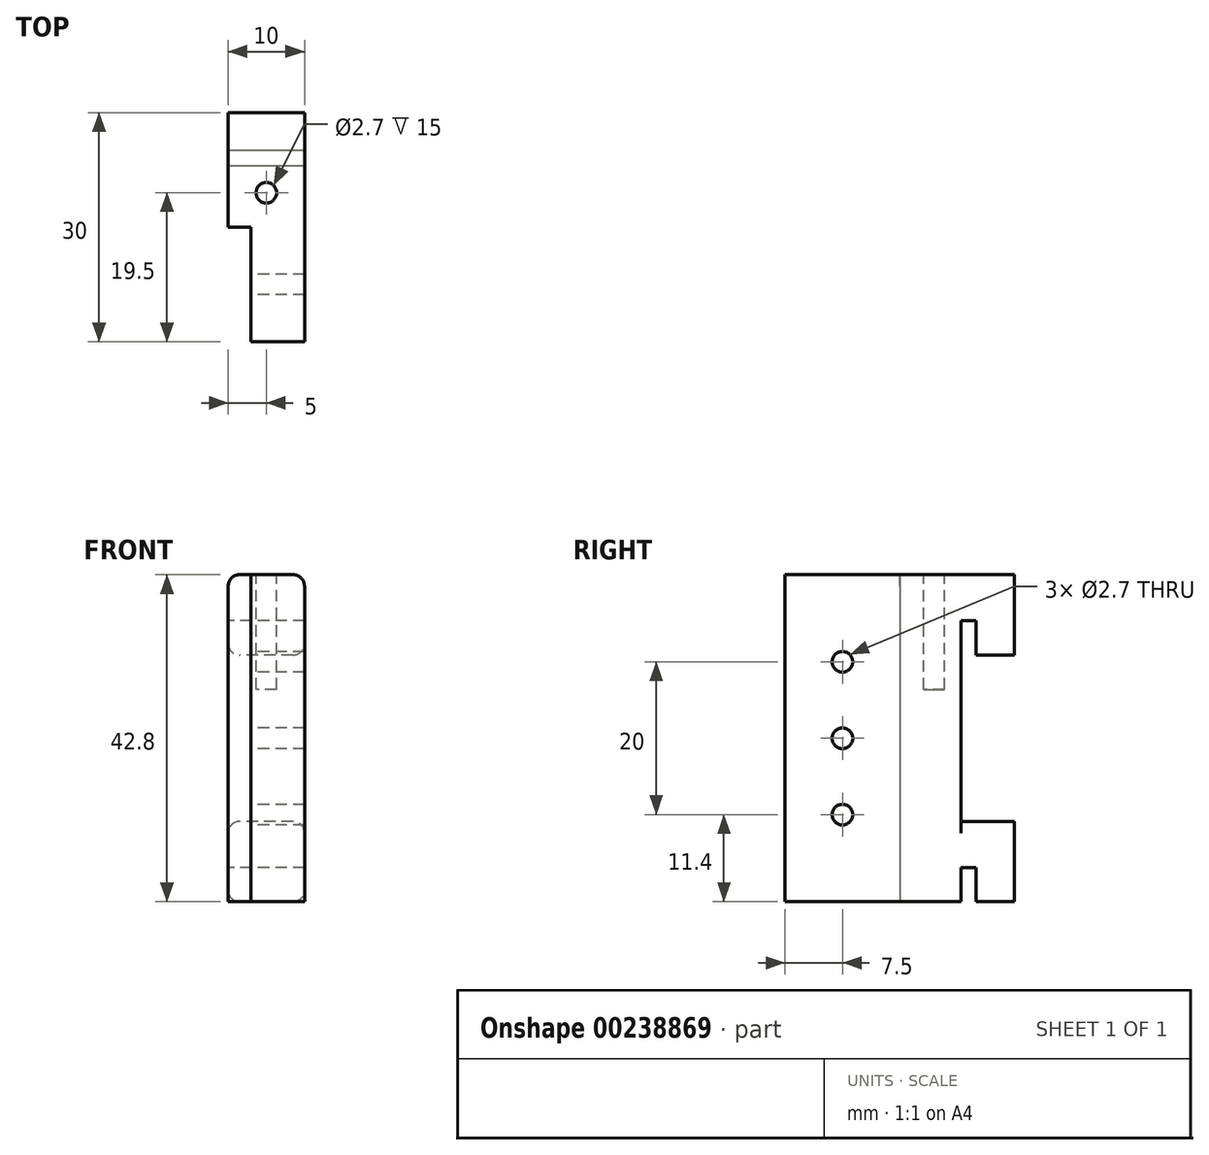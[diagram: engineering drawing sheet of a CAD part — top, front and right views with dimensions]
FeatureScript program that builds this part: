
annotation { "Feature Type Name" : "Feature", "Feature Type Description" : "" }
export const myFeature = defineFeature(function(context is Context, id is Id, definition is map)
    precondition{}
    {
        {
            var Q0;
            Q0=qCreatedBy(makeId("Right.planeOp"),FACE);
            var sketch = newSketch(context, id + "F0", { "sketchPlane" : qUnion([Q0])});
            skLineSegment(sketch, "E0", {"start": v(-23, 0) * mm, "end": v(-23, -42.8) * mm});
            skLineSegment(sketch, "E1", {"start": v(-23, -42.8) * mm, "end": v(0, -42.8) * mm});
            skLineSegment(sketch, "E2", {"start": v(0, -42.8) * mm, "end": v(0, -38.3) * mm});
            skLineSegment(sketch, "E3", {"start": v(0, -38.3) * mm, "end": v(2, -38.3) * mm});
            skLineSegment(sketch, "E4", {"start": v(2, -38.3) * mm, "end": v(2, -42.8) * mm});
            skLineSegment(sketch, "E5", {"start": v(2, -42.8) * mm, "end": v(7, -42.8) * mm});
            skLineSegment(sketch, "E6", {"start": v(7, -42.8) * mm, "end": v(7, -32.3) * mm});
            skLineSegment(sketch, "E7", {"start": v(7, -32.3) * mm, "end": v(0, -32.3) * mm});
            skLineSegment(sketch, "E8", {"start": v(0, -32.3) * mm, "end": v(0, -6) * mm});
            skLineSegment(sketch, "E9", {"start": v(0, -6) * mm, "end": v(2, -6) * mm});
            skLineSegment(sketch, "E10", {"start": v(2, -6) * mm, "end": v(2, -10.5) * mm});
            skLineSegment(sketch, "E11", {"start": v(2, -10.5) * mm, "end": v(7, -10.5) * mm});
            skLineSegment(sketch, "E12", {"start": v(7, -10.5) * mm, "end": v(7, 0) * mm});
            skLineSegment(sketch, "E13", {"start": v(7, 0) * mm, "end": v(-23, 0) * mm});
            skSolve(sketch);
        }
        {
            var Q0;
            Q0=qSketchRegion(id+"F0",true);
            extrude(context, id + "F1", {"entities" : qUnion([Q0]), "depth" : 10 * mm});
        }
        {
            var Q0;
            Q0=makeQuery(id+"F1.opExtrude","SWEPT_FACE",FACE,{"disambiguationData":[OSD([sQuery(id+"F0.wireOp",EDGE,"E13")])]});
            var sketch = newSketch(context, id + "F2", { "sketchPlane" : qUnion([Q0])});
            skLineSegment(sketch, "E14", {"start": v(5, 9.97) * mm, "end": v(5, -28.7) * mm, "construction": true});
            skPoint(sketch, "E14.startSnap0", {"position": v(5, 7) * mm});
            skCircle(sketch, "E15", {"center": v(5, -3.5) * mm, "radius": 1.35 * mm});
            skSolve(sketch);
        }
        {
            var Q0;
            Q0=qSketchRegion(id+"F2",true);
            extrude(context, id + "F3", {"entities" : qUnion([Q0]), "operationType" : NewBodyOperationType.REMOVE, "oppositeDirection" : true, "depth" : 15 * mm});
        }
        {
            var Q0;
            Q0=makeQuery(id+"F1.opExtrude","CAP_FACE",FACE,{"disambiguationData":[OSD([sQuery(id+"F0.wireOp",EDGE,"E0"),sQuery(id+"F0.wireOp",EDGE,"E1"),sQuery(id+"F0.wireOp",EDGE,"E2"),sQuery(id+"F0.wireOp",EDGE,"E3"),sQuery(id+"F0.wireOp",EDGE,"E4"),sQuery(id+"F0.wireOp",EDGE,"E5"),sQuery(id+"F0.wireOp",EDGE,"E6"),sQuery(id+"F0.wireOp",EDGE,"E7"),sQuery(id+"F0.wireOp",EDGE,"E8"),sQuery(id+"F0.wireOp",EDGE,"E9"),sQuery(id+"F0.wireOp",EDGE,"E10"),sQuery(id+"F0.wireOp",EDGE,"E11"),sQuery(id+"F0.wireOp",EDGE,"E12"),sQuery(id+"F0.wireOp",EDGE,"E13")])],"isStart":true});
            var sketch = newSketch(context, id + "F4", { "sketchPlane" : qUnion([Q0])});
            skLineSegment(sketch, "E16.bottom", {"start": v(23, 0) * mm, "end": v(8, 0) * mm});
            skLineSegment(sketch, "E16.top", {"start": v(23, -42.8) * mm, "end": v(8, -42.8) * mm});
            skLineSegment(sketch, "E16.left", {"start": v(23, 0) * mm, "end": v(23, -42.8) * mm});
            skLineSegment(sketch, "E16.right", {"start": v(8, 0) * mm, "end": v(8, -42.8) * mm});
            skSolve(sketch);
        }
        {
            var Q0;
            Q0 = qSketchRegion(id + "F4", true);
            extrude(context, id + "F5", {"entities" : qUnion([Q0]), "operationType" : NewBodyOperationType.REMOVE, "oppositeDirection" : true, "depth" : 3 * mm});
        }
        {
            var Q0;
            Q0=makeQuery(id+"F5.boolean.opBoolean","COPY",FACE,{"derivedFrom":makeQuery(id+"F5.opExtrude","CAP_FACE",FACE,{"disambiguationData":[OSD([sQuery(id+"F4.wireOp",EDGE,"E16.bottom"),sQuery(id+"F4.wireOp",EDGE,"E16.top"),sQuery(id+"F4.wireOp",EDGE,"E16.left"),sQuery(id+"F4.wireOp",EDGE,"E16.right")])],"isStart":false})});
            var sketch = newSketch(context, id + "F6", { "sketchPlane" : qUnion([Q0])});
            skLineSegment(sketch, "E17", {"start": v(15.5, 3.73) * mm, "end": v(15.5, -48.7) * mm, "construction": true});
            skPoint(sketch, "E17.startSnap0", {"position": v(15.5, 0) * mm});
            skPoint(sketch, "E17.endSnap0", {"position": v(15.5, -42.8) * mm});
            skCircle(sketch, "E18", {"center": v(15.5, -21.4) * mm, "radius": 1.35 * mm});
            skPoint(sketch, "E18.centerSnap0", {"position": v(23, -21.4) * mm});
            skCircle(sketch, "E19", {"center": v(15.5, -11.4) * mm, "radius": 1.35 * mm});
            skCircle(sketch, "E20", {"center": v(15.5, -31.4) * mm, "radius": 1.35 * mm});
            skSolve(sketch);
        }
        {
            var Q0;
            Q0 = qSketchRegion(id + "F6", true);
            extrude(context, id + "F7", {"entities" : qUnion([Q0]), "operationType" : NewBodyOperationType.REMOVE, "endBound" : BoundingType.THROUGH_ALL, "oppositeDirection" : true, "depth" : 25 * mm});
        }
        {
            var Q0;
            Q0=makeQuery(id+"F1.opExtrude","CAP_EDGE",EDGE,{"disambiguationData":[OSD([sQuery(id+"F0.wireOp",EDGE,"E13")])],"isStart":true});
            var Q1;
            Q1=makeQuery(id+"F1.opExtrude","CAP_EDGE",EDGE,{"disambiguationData":[OSD([sQuery(id+"F0.wireOp",EDGE,"E13")])],"isStart":false});
            var Q2;
            Q2=makeQuery(id+"F1.opExtrude","CAP_EDGE",EDGE,{"disambiguationData":[OSD([sQuery(id+"F0.wireOp",EDGE,"E11")])],"isStart":true});
            var Q3;
            Q3=makeQuery(id+"F1.opExtrude","CAP_EDGE",EDGE,{"disambiguationData":[OSD([sQuery(id+"F0.wireOp",EDGE,"E7")])],"isStart":true});
            var Q4;
            Q4=makeQuery(id+"F1.opExtrude","CAP_EDGE",EDGE,{"disambiguationData":[OSD([sQuery(id+"F0.wireOp",EDGE,"E7")])],"isStart":false});
            var Q5;
            Q5=makeQuery(id+"F1.opExtrude","CAP_EDGE",EDGE,{"disambiguationData":[OSD([sQuery(id+"F0.wireOp",EDGE,"E11")])],"isStart":false});
            var Q6;
            Q6=makeQuery(id+"F1.opExtrude","CAP_EDGE",EDGE,{"disambiguationData":[OSD([sQuery(id+"F0.wireOp",EDGE,"E5")])],"isStart":false});
            var Q7;
            Q7=makeQuery(id+"F1.opExtrude","CAP_EDGE",EDGE,{"disambiguationData":[OSD([sQuery(id+"F0.wireOp",EDGE,"E5")])],"isStart":true});
            fillet(context, id + "F8", {"entities" : qUnion([Q0, Q1, Q2, Q3, Q4, Q5, Q6, Q7]), "radius" : 1.5 * mm, "tangentPropagation" : true, "allowEdgeOverflow" : false});
        }
    });
